# Revit family: Ghent - Flyte Frameless Whiteboard
name_source: partatom
category: Furniture
units: mm (PartAtom-declared; Revit-internal decimal feet)

## family parameters
Cut with Voids When Loaded = No
Host = Face
Room Calculation Point = No
Shared = No

## types (16) — shared parameters
Default Elevation = 4' - 0"
Manufacturer = Ghent
URL = https://ghent.com

## per-type parameters (varying)
| type | Height | Model | Width |
| Duo - 18″ × 24″ | 1' - 6" | FLYD1824 | 1' - 11 15/16" |
| Duo - 24″ × 36″ | 1' - 11 15/16" | FLYD2436 | 3' - 0" |
| Duo - 36″ × 48″ | 3' - 0" | FLYD3648 | 4' - 0" |
| Duo - 48″ × 48″ | 4' - 0" | FLYD4848 | 4' - 0" |
| Duo - 48″ × 60″ | 4' - 0" | FLYD4860 | 5' - 0" |
| Duo - 48″ × 72″ | 4' - 0" | FLYD4872 | 6' - 0 1/16" |
| Duo - 48″ × 84″ | 4' - 0" | FLYD4884 | 7' - 0" |
| Duo - 48″ × 96″ | 4' - 0" | FLYD4896 | 8' - 0 1/8" |
| Solo - 18″ × 24″ | 1' - 6" | FLYS1824 | 1' - 11 15/16" |
| Solo - 24″ × 36″ | 1' - 11 15/16" | FLYS2436 | 3' - 0" |
| Solo - 36″ × 48″ | 3' - 0" | FLYS3648 | 4' - 0" |
| Solo - 48″ × 48″ | 4' - 0" | FLYS4848 | 4' - 0" |
| Solo - 48″ × 60″ | 4' - 0" | FLYS4860 | 5' - 0" |
| Solo - 48″ × 72″ | 4' - 0" | FLYS4872 | 6' - 0 1/16" |
| Solo - 48″ × 84″ | 4' - 0" | FLYS4884 | 7' - 0" |
| Solo - 48″ × 96″ | 4' - 0" | FLYS4896 | 8' - 0 1/8" |

## geometry (parser evidence)
native form markers: Sweep x2
no freeform markers — native parametric forms only
